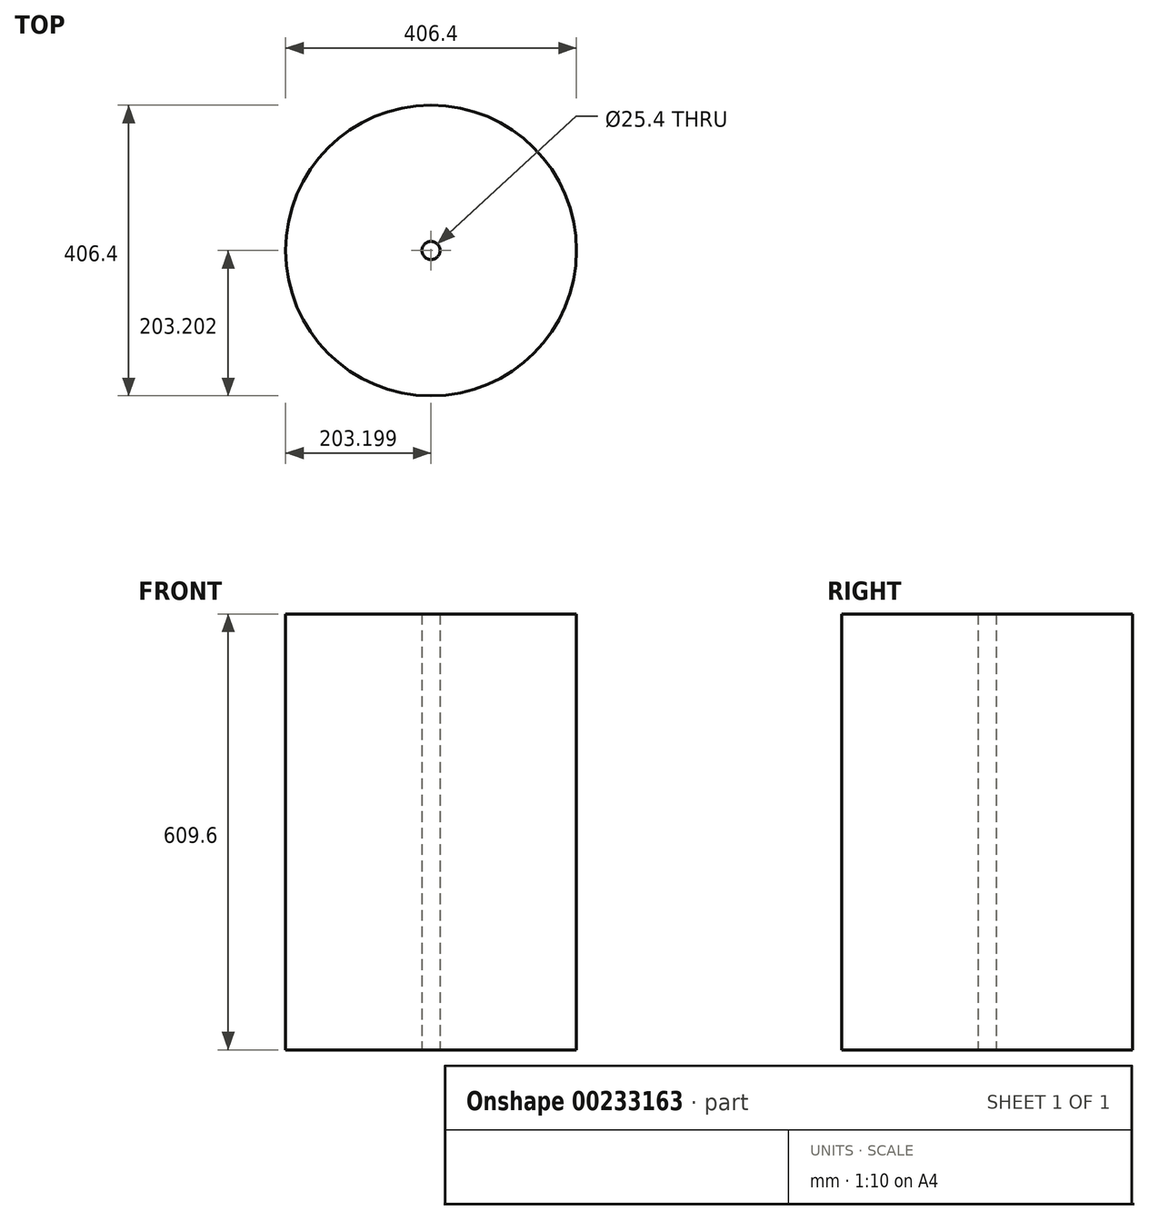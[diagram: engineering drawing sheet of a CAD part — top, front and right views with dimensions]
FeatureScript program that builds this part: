
annotation { "Feature Type Name" : "Feature", "Feature Type Description" : "" }
export const myFeature = defineFeature(function(context is Context, id is Id, definition is map)
    precondition{}
    {
        {
            var Q0;
            Q0=qCreatedBy(makeId("Top.planeOp"),FACE);
            var sketch = newSketch(context, id + "F0", { "sketchPlane" : qUnion([Q0])});
            skCircle(sketch, "E0", {"center": v(-46.04, 39.02) * mm, "radius": 203.2 * mm});
            skCircle(sketch, "E1", {"center": v(-46.04, 39.02) * mm, "radius": 12.7 * mm});
            skSolve(sketch);
        }
        {
            var Q0;
            Q0=makeQuery(id+"F0.imprint","IMPRINT",FACE,{"disambiguationData":[TD([[makeQuery(id+"F0.imprint","IMPRINT",EDGE,{"derivedFrom":sQuery(id+"F0.wireOp",EDGE,"E0")}),1.0]])]});
            extrude(context, id + "F1", {"entities" : qUnion([Q0]), "depth" : 609.6 * mm});
        }
    });
